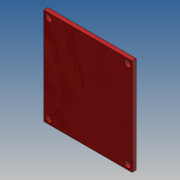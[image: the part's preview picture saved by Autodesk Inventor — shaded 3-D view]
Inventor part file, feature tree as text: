
AUTODESK INVENTOR PART (.ipt)
format: ipt  version: 2017 (Build 210142000, 142)  size: 96,256 bytes
history: native  units: mm
features: other x1, extrude x1, sketch x1
ambient origin geometry x8: Origin, YZ Plane, XZ Plane, XY Plane, X Axis, Y Axis, Z Axis, Center Point
bodies: Body1 (feature_tree)
feature tree (3):
  other  "Sólido1"
  extrude  "Extrusión1"  Depth=2.0mm
  sketch  "Boceto1"  dims[d0=3.0mm d1=2.25mm d2=47.0mm d3=43.0mm d4=2.0mm d5=0.0mm d6=42.5mm d7=38.5mm]
